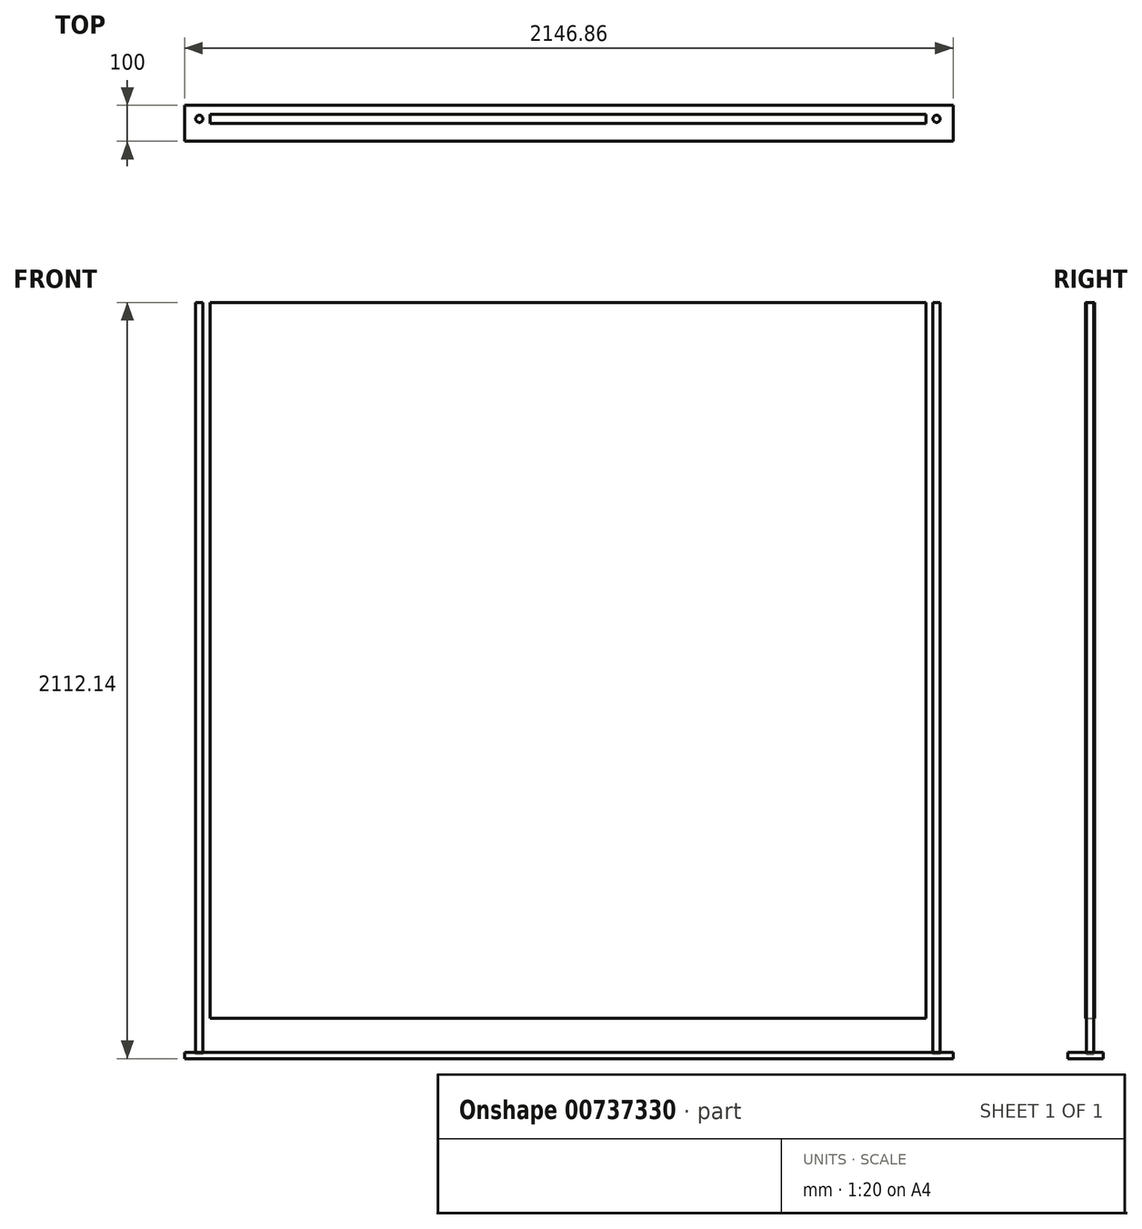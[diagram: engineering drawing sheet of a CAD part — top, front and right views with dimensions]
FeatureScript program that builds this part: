
annotation { "Feature Type Name" : "Feature", "Feature Type Description" : "" }
export const myFeature = defineFeature(function(context is Context, id is Id, definition is map)
    precondition{}
    {
        {
            var Q0;
            Q0=qCreatedBy(makeId("Front.planeOp"),FACE);
            var sketch = newSketch(context, id + "F0", { "sketchPlane" : qUnion([Q0])});
            skLineSegment(sketch, "E0.bottom", {"start": v(-1008.67, 1169.99) * mm, "end": v(991.33, 1169.99) * mm});
            skLineSegment(sketch, "E0.top", {"start": v(-1008.67, -830.01) * mm, "end": v(991.33, -830.01) * mm});
            skLineSegment(sketch, "E0.left", {"start": v(-1008.67, 1169.99) * mm, "end": v(-1008.67, -830.01) * mm});
            skLineSegment(sketch, "E0.right", {"start": v(991.33, 1169.99) * mm, "end": v(991.33, -830.01) * mm});
            skSolve(sketch);
        }
        {
            var Q0;
            Q0 = qSketchRegion(id + "F0", true);
            extrude(context, id + "F1", {"entities" : qUnion([Q0]), "depth" : 25 * mm, "offsetDistance" : 25 * mm});
        }
        {
            var Q0;
            Q0=makeQuery(id+"F1.opExtrude","SWEPT_FACE",FACE,{"disambiguationData":[OSD([sQuery(id+"F0.wireOp",EDGE,"E0.bottom")])]});
            var sketch = newSketch(context, id + "F2", { "sketchPlane" : qUnion([Q0])});
            skCircle(sketch, "E1", {"center": v(-1038.67, -12.5) * mm, "radius": 10 * mm});
            skPoint(sketch, "E1.centerSnap0", {"position": v(-1008.67, -12.5) * mm});
            skCircle(sketch, "E2", {"center": v(1021.33, -12.5) * mm, "radius": 10 * mm});
            skPoint(sketch, "E2.centerSnap0", {"position": v(991.33, -12.5) * mm});
            skSolve(sketch);
        }
        {
            var Q0;
            Q0 = qSketchRegion(id + "F2", true);
            extrude(context, id + "F3", {"entities" : qUnion([Q0]), "oppositeDirection" : true, "depth" : 2100 * mm, "offsetDistance" : 25 * mm});
        }
        {
            var Q0;
            Q0=makeQuery(id+"F1.opExtrude","CAP_FACE",FACE,{"disambiguationData":[OSD([sQuery(id+"F0.wireOp",EDGE,"E0.bottom"),sQuery(id+"F0.wireOp",EDGE,"E0.top"),sQuery(id+"F0.wireOp",EDGE,"E0.left"),sQuery(id+"F0.wireOp",EDGE,"E0.right")])],"isStart":false});
            var sketch = newSketch(context, id + "F4", { "sketchPlane" : qUnion([Q0])});
            skLineSegment(sketch, "E3.bottom", {"start": v(-1079.53, -924.32) * mm, "end": v(1067.33, -924.32) * mm});
            skLineSegment(sketch, "E3.top", {"start": v(-1079.53, -942.15) * mm, "end": v(1067.33, -942.15) * mm});
            skLineSegment(sketch, "E3.left", {"start": v(-1079.53, -924.32) * mm, "end": v(-1079.53, -942.15) * mm});
            skLineSegment(sketch, "E3.right", {"start": v(1067.33, -924.32) * mm, "end": v(1067.33, -942.15) * mm});
            skSolve(sketch);
        }
        {
            var Q0;
            Q0 = qSketchRegion(id + "F4", true);
            extrude(context, id + "F5", {"entities" : qUnion([Q0]), "oppositeDirection" : true, "depth" : 50 * mm, "offsetDistance" : 25 * mm, "hasSecondDirection" : true, "secondDirectionOppositeDirection" : false, "secondDirectionDepth" : 50 * mm});
        }
    });
